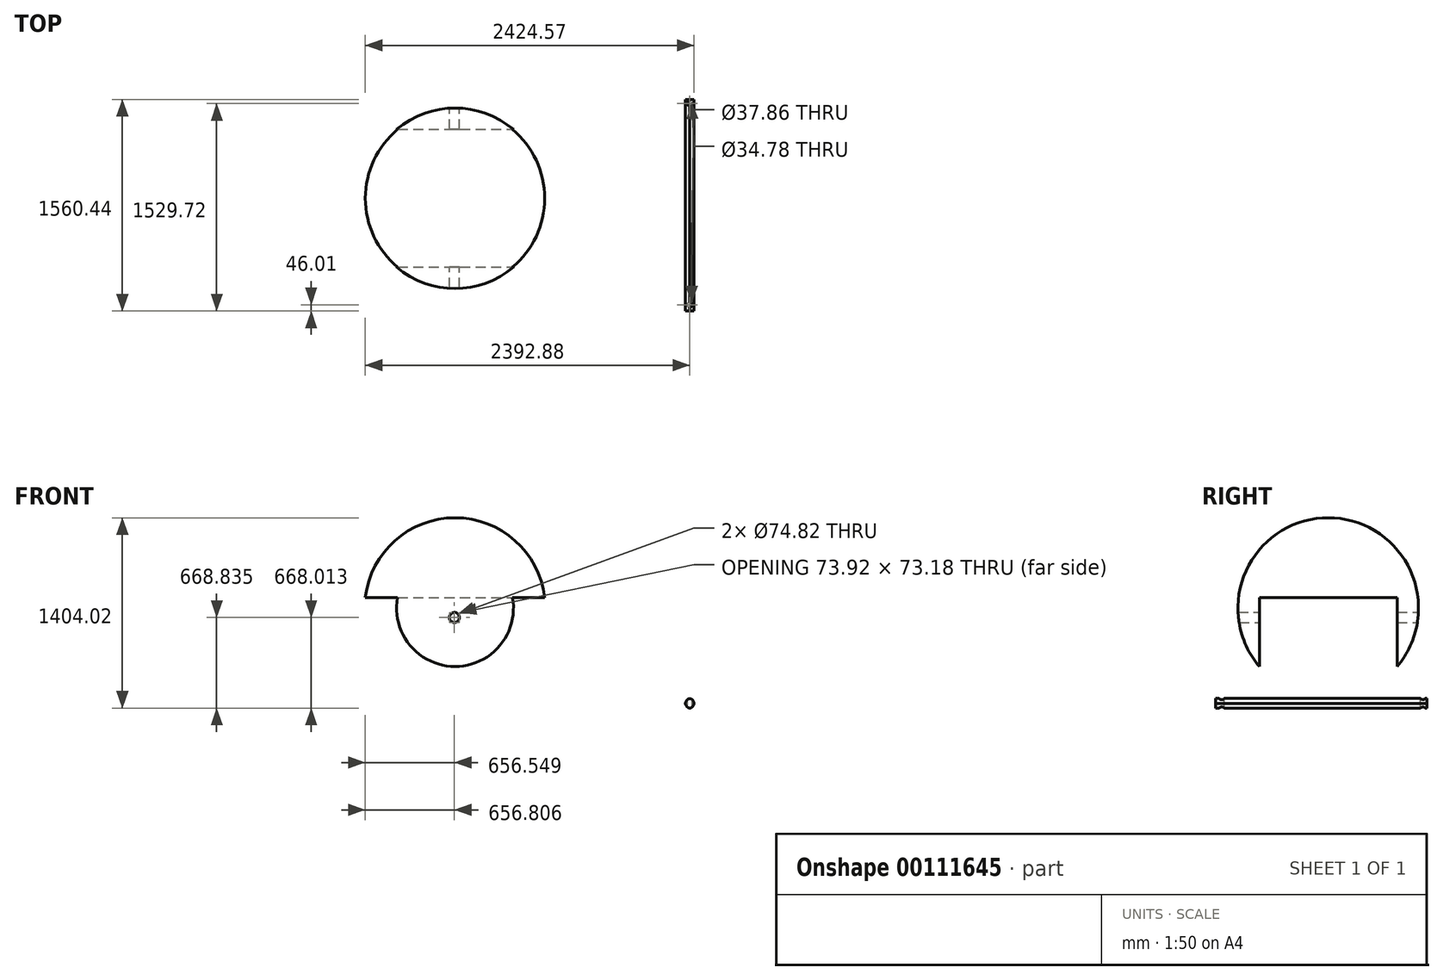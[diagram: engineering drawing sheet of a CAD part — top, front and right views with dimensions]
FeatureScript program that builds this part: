
annotation { "Feature Type Name" : "Feature", "Feature Type Description" : "" }
export const myFeature = defineFeature(function(context is Context, id is Id, definition is map)
    precondition{}
    {
        {
            var Q0;
            Q0=qCreatedBy(makeId("Front.planeOp"),FACE);
            var sketch = newSketch(context, id + "F0", { "sketchPlane" : qUnion([Q0])});
            skArc(sketch, "E0", {"start": v(-1033.43, -382.42) * mm, "mid": v(-1699.57, 283.72) * mm, "end": v(-2365.72, -382.42) * mm});
            skLineSegment(sketch, "E1", {"start": v(-1699.57, -382.42) * mm, "end": v(-2365.72, -382.42) * mm});
            skLineSegment(sketch, "E2", {"start": v(-1699.57, -382.42) * mm, "end": v(-1033.43, -382.42) * mm});
            skSolve(sketch);
        }
        {
            var Q0;
            Q0 = qSketchRegion(id + "F0", true);
            var Q1;
            Q1=sQuery(id+"F0.wireOp",EDGE,"E2");
            revolve(context, id + "F1", {"entities" : qUnion([Q0]), "axis" : qUnion([Q1]), "revolveType" : RevolveType.FULL});
        }
        {
            var Q0;
            Q0=qCreatedBy(makeId("Front.planeOp"),FACE);
            var sketch = newSketch(context, id + "F2", { "sketchPlane" : qUnion([Q0])});
            skLineSegment(sketch, "E3.bottom", {"start": v(-2789.87, -304.35) * mm, "end": v(-488.63, -304.35) * mm});
            skLineSegment(sketch, "E3.top", {"start": v(-2789.87, -1271.81) * mm, "end": v(-488.63, -1271.81) * mm});
            skLineSegment(sketch, "E3.left", {"start": v(-2789.87, -304.35) * mm, "end": v(-2789.87, -1271.81) * mm});
            skLineSegment(sketch, "E3.right", {"start": v(-488.63, -304.35) * mm, "end": v(-488.63, -1271.81) * mm});
            skSolve(sketch);
        }
        {
            var Q0;
            Q0 = qSketchRegion(id + "F2", true);
            extrude(context, id + "F3", {"entities" : qUnion([Q0]), "operationType" : NewBodyOperationType.REMOVE, "oppositeDirection" : true, "depth" : 508 * mm, "hasSecondDirection" : true, "secondDirectionOppositeDirection" : false, "secondDirectionDepth" : 508 * mm});
        }
        {
            var Q0;
            Q0=qCreatedBy(makeId("Right.planeOp"),FACE);
            var sketch = newSketch(context, id + "F4", { "sketchPlane" : qUnion([Q0])});
            skLineSegment(sketch, "E4.bottom", {"start": v(-831.41, -1048.85) * mm, "end": v(729.03, -1048.85) * mm});
            skLineSegment(sketch, "E4.top", {"start": v(-831.41, -1120.83) * mm, "end": v(729.03, -1120.83) * mm});
            skLineSegment(sketch, "E4.left", {"start": v(-831.41, -1048.85) * mm, "end": v(-831.41, -1120.83) * mm});
            skLineSegment(sketch, "E4.right", {"start": v(729.03, -1048.85) * mm, "end": v(729.03, -1120.83) * mm});
            skSolve(sketch);
        }
        {
            var Q0;
            Q0 = qSketchRegion(id + "F4", true);
            extrude(context, id + "F5", {"entities" : qUnion([Q0]), "depth" : 63.5 * mm});
        }
        {
            var Q0;
            Q0=qCreatedBy(makeId("Front.planeOp"),FACE);
            var sketch = newSketch(context, id + "F6", { "sketchPlane" : qUnion([Q0])});
            skCircle(sketch, "E5", {"center": v(-1704.32, -451.46) * mm, "radius": 37.41 * mm});
            skSolve(sketch);
        }
        {
            var Q0;
            Q0 = qSketchRegion(id + "F6", true);
            extrude(context, id + "F7", {"entities" : qUnion([Q0]), "operationType" : NewBodyOperationType.REMOVE, "endBound" : BoundingType.SYMMETRIC, "depth" : 1905 * mm});
        }
        {
            var Q0;
            Q0=makeQuery(id+"F5.opExtrude","SWEPT_FACE",FACE,{"disambiguationData":[OSD([sQuery(id+"F4.wireOp",EDGE,"E4.bottom")])]});
            var sketch = newSketch(context, id + "F8", { "sketchPlane" : qUnion([Q0])});
            skCircle(sketch, "E6", {"center": v(31.75, -785.4) * mm, "radius": 18.93 * mm});
            skPoint(sketch, "E6.centerSnap0", {"position": v(31.75, -831.41) * mm});
            skCircle(sketch, "E7", {"center": v(31.75, 698.3) * mm, "radius": 17.4 * mm});
            skPoint(sketch, "E7.centerSnap0", {"position": v(31.75, 729.03) * mm});
            skSolve(sketch);
        }
        {
            var Q0;
            Q0=makeQuery(id+"F8.imprint","IMPRINT",FACE,{"disambiguationData":[TD([[makeQuery(id+"F8.imprint","IMPRINT",EDGE,{"derivedFrom":sQuery(id+"F8.wireOp",EDGE,"E7")}),1.0]])]});
            var Q1;
            Q1=makeQuery(id+"F8.imprint","IMPRINT",FACE,{"disambiguationData":[TD([[makeQuery(id+"F8.imprint","IMPRINT",EDGE,{"derivedFrom":sQuery(id+"F8.wireOp",EDGE,"E6")}),1.0]])]});
            var Q2;
            Q2=sQuery(id+"F8.wireOp",EDGE,"E7");
            var Q3;
            Q3=sQuery(id+"F8.wireOp",EDGE,"E6");
            extrude(context, id + "F9", {"entities" : qUnion([Q0, Q1]), "operationType" : NewBodyOperationType.REMOVE, "surfaceEntities" : qUnion([Q2, Q3]), "oppositeDirection" : true, "depth" : 254 * mm});
        }
        {
            var Q0;
            Q0=makeQuery(id+"F5.opExtrude","CAP_EDGE",EDGE,{"disambiguationData":[OSD([sQuery(id+"F4.wireOp",EDGE,"E4.bottom")])],"isStart":false});
            var Q1;
            Q1=makeQuery(id+"F5.opExtrude","CAP_EDGE",EDGE,{"disambiguationData":[OSD([sQuery(id+"F4.wireOp",EDGE,"E4.top")])],"isStart":false});
            var Q2;
            Q2=makeQuery(id+"F5.opExtrude","CAP_EDGE",EDGE,{"disambiguationData":[OSD([sQuery(id+"F4.wireOp",EDGE,"E4.top")])],"isStart":true});
            var Q3;
            Q3=makeQuery(id+"F5.opExtrude","CAP_EDGE",EDGE,{"disambiguationData":[OSD([sQuery(id+"F4.wireOp",EDGE,"E4.bottom")])],"isStart":true});
            fillet(context, id + "F10", {"entities" : qUnion([Q0, Q1, Q2, Q3]), "radius" : 38.1 * mm, "tangentPropagation" : true, "allowEdgeOverflow" : false});
        }
    });
